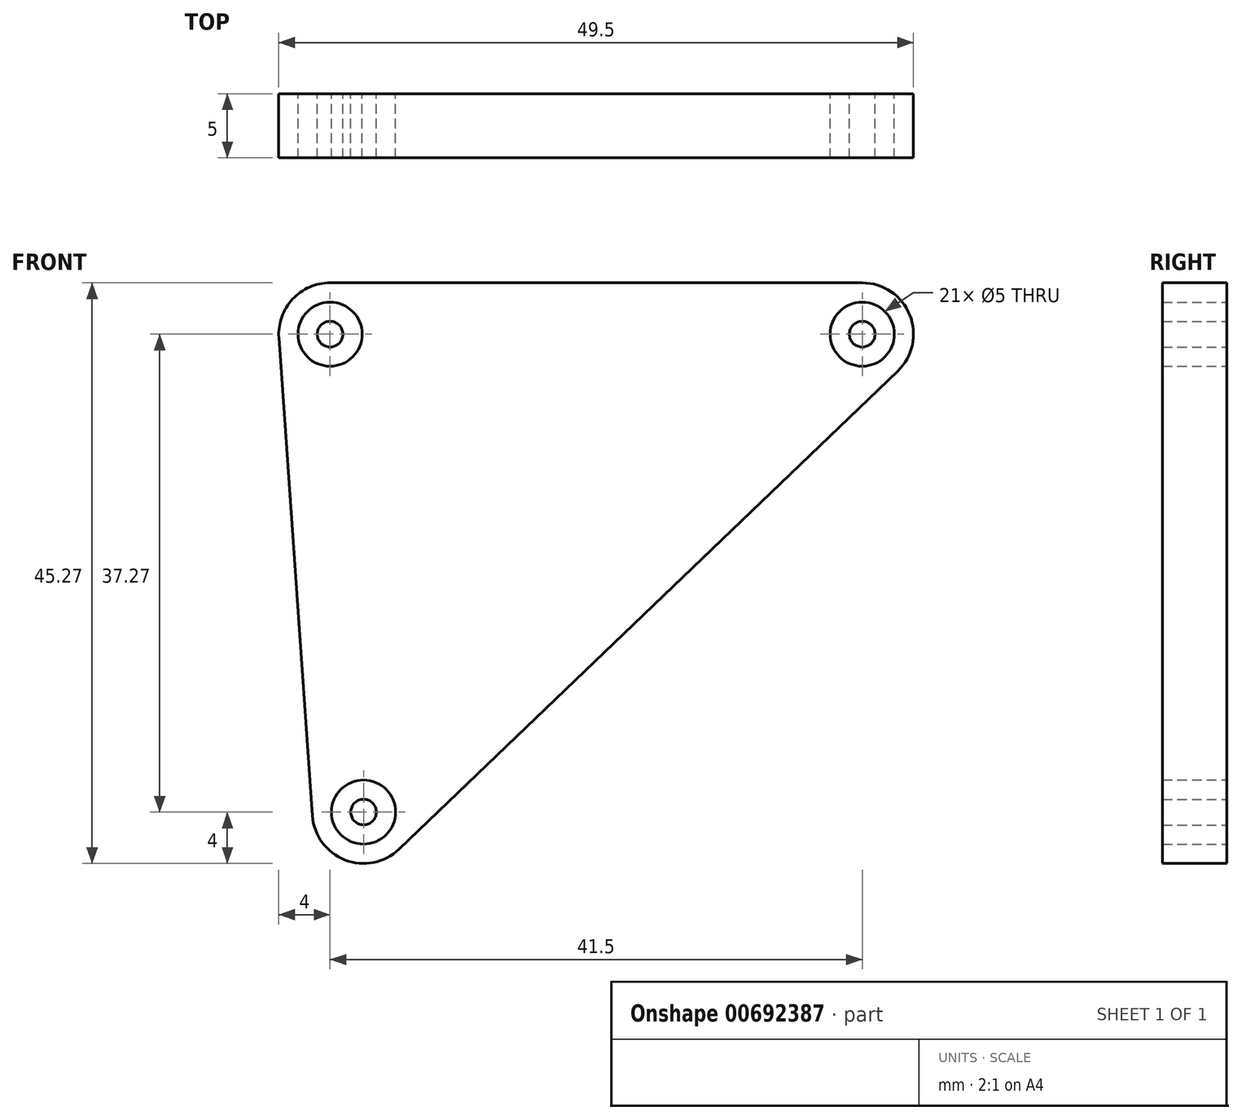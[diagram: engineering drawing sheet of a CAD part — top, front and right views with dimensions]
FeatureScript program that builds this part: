
annotation { "Feature Type Name" : "Feature", "Feature Type Description" : "" }
export const myFeature = defineFeature(function(context is Context, id is Id, definition is map)
    precondition{}
    {
        {
            var Q0;
            Q0=qCreatedBy(makeId("Front.planeOp"),FACE);
            var sketch = newSketch(context, id + "F0", { "sketchPlane" : qUnion([Q0])});
            skArc(sketch, "E0", {"start": v(-17.1, -34.8) * mm, "mid": v(-14.54, -38.26) * mm, "end": v(-10.33, -37.42) * mm});
            skArc(sketch, "E1", {"start": v(-15.71, 6.74) * mm, "mid": v(-18.64, 5.47) * mm, "end": v(-19.7, 2.46) * mm});
            skArc(sketch, "E2", {"start": v(28.56, -0.15) * mm, "mid": v(29.5, 4.23) * mm, "end": v(25.79, 6.74) * mm});
            skLineSegment(sketch, "E3", {"start": v(-19.7, 2.46) * mm, "end": v(-17.1, -34.8) * mm});
            skLineSegment(sketch, "E4", {"start": v(-15.71, 6.74) * mm, "end": v(25.79, 6.74) * mm});
            skLineSegment(sketch, "E5", {"start": v(-10.33, -37.42) * mm, "end": v(28.56, -0.15) * mm});
            skCircle(sketch, "E6", {"center": v(-15.71, 2.74) * mm, "radius": 2.5 * mm});
            skCircle(sketch, "E7", {"center": v(-13.1, -34.53) * mm, "radius": 2.5 * mm});
            skCircle(sketch, "E8", {"center": v(25.79, 2.74) * mm, "radius": 2.5 * mm});
            skCircle(sketch, "E9", {"center": v(-15.71, 2.74) * mm, "radius": 1 * mm});
            skCircle(sketch, "E10", {"center": v(-13.1, -34.53) * mm, "radius": 1 * mm});
            skCircle(sketch, "E11", {"center": v(25.79, 2.74) * mm, "radius": 1 * mm});
            skSolve(sketch);
        }
        {
            var Q0;
            Q0 = qSketchRegion(id + "F0", true);
            var Q1;
            Q1=makeQuery(id+"F0.imprint","IMPRINT",FACE,{"disambiguationData":[TD([[makeQuery(id+"F0.imprint","IMPRINT",EDGE,{"derivedFrom":sQuery(id+"F0.wireOp",EDGE,"E9")}),1.0]])]});
            var Q2;
            Q2=makeQuery(id+"F0.imprint","IMPRINT",FACE,{"disambiguationData":[TD([[makeQuery(id+"F0.imprint","IMPRINT",EDGE,{"derivedFrom":sQuery(id+"F0.wireOp",EDGE,"E11")}),1.0]])]});
            var Q3;
            Q3=makeQuery(id+"F0.imprint","IMPRINT",FACE,{"disambiguationData":[TD([[makeQuery(id+"F0.imprint","IMPRINT",EDGE,{"derivedFrom":sQuery(id+"F0.wireOp",EDGE,"E10")}),1.0]])]});
            extrude(context, id + "F1", {"entities" : qUnion([Q0, Q1, Q2, Q3]), "depth" : 5 * mm, "offsetDistance" : 25 * mm});
        }
    });
